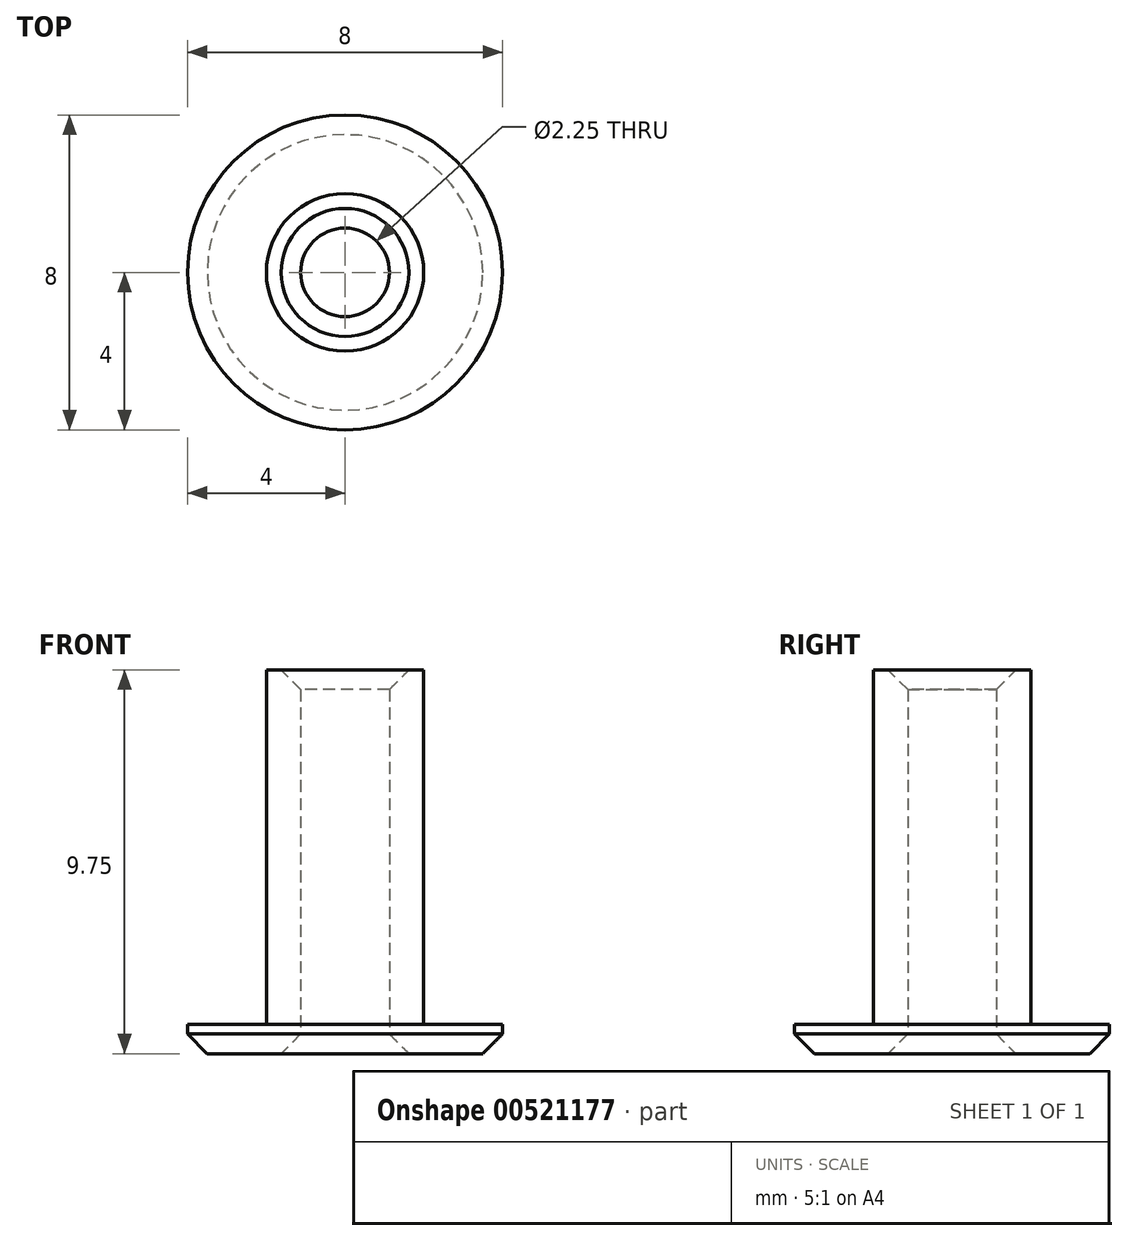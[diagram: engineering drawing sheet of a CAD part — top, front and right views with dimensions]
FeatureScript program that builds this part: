
annotation { "Feature Type Name" : "Feature", "Feature Type Description" : "" }
export const myFeature = defineFeature(function(context is Context, id is Id, definition is map)
    precondition{}
    {
        {
            var Q0;
            Q0=qCreatedBy(makeId("Top.planeOp"),FACE);
            var sketch = newSketch(context, id + "F0", { "sketchPlane" : qUnion([Q0])});
            skCircle(sketch, "E0", {"center": v(0, 0) * mm, "radius": 2 * mm});
            skCircle(sketch, "E1", {"center": v(0, 0) * mm, "radius": 1.13 * mm});
            skCircle(sketch, "E2", {"center": v(0, 0) * mm, "radius": 4 * mm});
            skSolve(sketch);
        }
        {
            var Q0;
            Q0=makeQuery(id+"F0.imprint","IMPRINT",FACE,{"disambiguationData":[TD([[makeQuery(id+"F0.imprint","IMPRINT",EDGE,{"derivedFrom":sQuery(id+"F0.wireOp",EDGE,"E0")}),1.0]])]});
            extrude(context, id + "F1", {"entities" : qUnion([Q0]), "depth" : 9 * mm, "offsetDistance" : 25 * mm});
        }
        {
            var Q0;
            Q0=makeQuery(id+"F0.imprint","IMPRINT",FACE,{"disambiguationData":[TD([[makeQuery(id+"F0.imprint","IMPRINT",EDGE,{"derivedFrom":sQuery(id+"F0.wireOp",EDGE,"E0")}),-1.0]])]});
            var Q1;
            Q1=makeQuery(id+"F0.imprint","IMPRINT",FACE,{"disambiguationData":[TD([[makeQuery(id+"F0.imprint","IMPRINT",EDGE,{"derivedFrom":sQuery(id+"F0.wireOp",EDGE,"E0")}),1.0]])]});
            extrude(context, id + "F2", {"entities" : qUnion([Q0, Q1]), "operationType" : NewBodyOperationType.ADD, "oppositeDirection" : true, "depth" : 0.75 * mm, "offsetDistance" : 25 * mm});
        }
        {
            var Q0;
            {var subQ0=sQuery(id+"F0.wireOp",EDGE,"E1");Q0=makeQuery(id+"F2.boolean.opBoolean","MERGE",FACE,{"derivedFrom":[makeQuery(id+"F1.opExtrude","SWEPT_FACE",FACE,{"disambiguationData":[OSD([subQ0])]}),makeQuery(id+"F2.opExtrude","SWEPT_FACE",FACE,{"disambiguationData":[OSD([subQ0])]})]});}
            var Q1;
            Q1=makeQuery(id+"F2.opExtrude","CAP_EDGE",EDGE,{"disambiguationData":[OSD([sQuery(id+"F0.wireOp",EDGE,"E2")])],"isStart":false});
            chamfer(context, id + "F3", {"entities" : qUnion([Q0, Q1]), "width" : 0.5 * mm, "tangentPropagation" : true});
        }
    });
